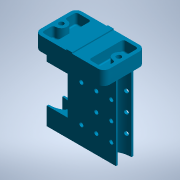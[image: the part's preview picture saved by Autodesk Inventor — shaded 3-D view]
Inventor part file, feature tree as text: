
AUTODESK INVENTOR PART (.ipt)
format: ipt  version: 2020 (Build 240168000, 168)  size: 404,992 bytes
history: native  units: mm
features: sketch x8, extrude x6, fillet x5, hole x2, mirror x2
ambient origin geometry x8: Origin, YZ Plane, XZ Plane, XY Plane, X Axis, Y Axis, Z Axis, Center Point
bodies: Solid1 (feature_tree)
feature tree (23):
  extrude  "Extrusion1"  Depth=30.0mm
  hole  "Hole1"  [1 undecoded]
  fillet  "Fillet1"  Radius=1.0mm
  extrude  "Extrusion3"  Depth=10.0mm TaperAngle=0.0deg
  fillet  "Fillet2"  Radius=5.0mm
  fillet  "Fillet3"  Radius=3.0mm
  fillet  "Fillet4"  Radius=3.0mm
  fillet  "Fillet5"  Radius=5.0mm
  mirror  "Mirror3"
  mirror  "Mirror2"
  extrude  "Extrusion2"  Depth=18.0mm
  extrude  "Extrusion4"  Depth=18.0mm TaperAngle=0.0deg
  extrude  "Extrusion5"  Depth=18.0mm
  hole  "Perçage3"  [1 undecoded]
  extrude  "Extrusion6"  Depth=5.0mm
  sketch  "Sketch1"  dims[d0=36.0mm d1=30.0mm]
  sketch  "Sketch2"  dims[d3=12.0mm d4=0.0mm d5=25.0mm]
  sketch  "Sketch4"  dims[d6=4.2mm d7=6.0mm d8=4.0mm d9=2.0mm d10=90.0deg d11=8.0mm d12=20.594885mm d22=1.0mm]
  sketch  "Sketch5"  dims[d23=5.0mm d24=10.0mm d25=0.0mm d26=5.0mm d27=3.0mm d28=3.0mm d29=5.0mm]
  sketch  "Sketch6"  dims[d30=14.0mm d31=6.0mm d32=9.0mm d33=0.0mm d34=2.0mm d35=2.0mm d36=5.0mm d37=1.0mm d38=64.0mm d40=15.0mm d42=10.5mm d44=60.0mm d45=0.0mm d47=10.0mm d48=0.0mm d58=12.0mm d59=6.0mm d62=16.0mm d63=13.0mm d65=17.0mm d66=16.0mm d67=13.0mm d68=3.5mm d69=6.0mm d70=4.0mm d71=2.0mm d72=90.0deg d73=8.0mm d74=20.594885mm d76=64.0mm d82=33.0mm d83=18.0mm d84=27.5mm d85=0.0mm d86=0.0mm d87=32.0mm]
  sketch  "Esquisse10"
  sketch  "Esquisse11"
  sketch  "Esquisse13"
note: 2 required parameter values undecoded (feature->parameter linkage not recoverable at this tier; creation-order binding heuristic only, values carry confidence <= 0.55)
